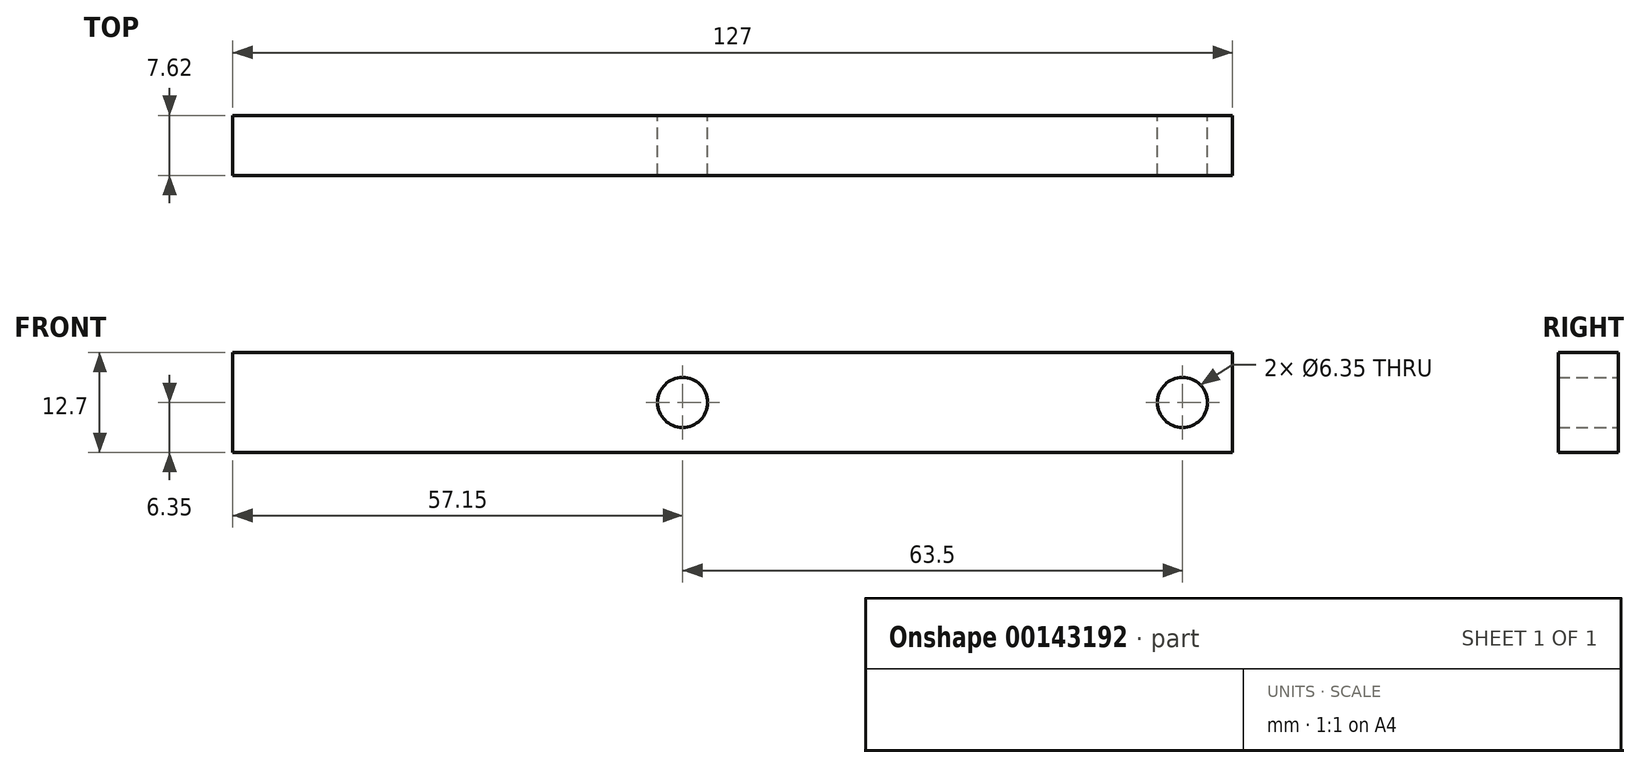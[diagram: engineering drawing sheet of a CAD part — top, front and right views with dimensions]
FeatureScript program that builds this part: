
annotation { "Feature Type Name" : "Feature", "Feature Type Description" : "" }
export const myFeature = defineFeature(function(context is Context, id is Id, definition is map)
    precondition{}
    {
        {
            var Q0;
            Q0=qCreatedBy(makeId("Front.planeOp"),FACE);
            var sketch = newSketch(context, id + "F0", { "sketchPlane" : qUnion([Q0])});
            skLineSegment(sketch, "E0.bottom", {"start": v(0, 0) * mm, "end": v(127, 0) * mm});
            skLineSegment(sketch, "E0.top", {"start": v(0, 12.7) * mm, "end": v(127, 12.7) * mm});
            skLineSegment(sketch, "E0.left", {"start": v(0, 0) * mm, "end": v(0, 12.7) * mm});
            skLineSegment(sketch, "E0.right", {"start": v(127, 0) * mm, "end": v(127, 12.7) * mm});
            skCircle(sketch, "E1", {"center": v(57.15, 6.35) * mm, "radius": 3.18 * mm});
            skCircle(sketch, "E2", {"center": v(120.65, 6.35) * mm, "radius": 3.18 * mm});
            skSolve(sketch);
        }
        {
            var Q0;
            Q0=makeQuery(id+"F0.imprint","IMPRINT",FACE,{"disambiguationData":[TD([[makeQuery(id+"F0.imprint","IMPRINT",EDGE,{"derivedFrom":sQuery(id+"F0.wireOp",EDGE,"E0.bottom")}),1.0]])]});
            extrude(context, id + "F1", {"entities" : qUnion([Q0]), "depth" : 7.62 * mm});
        }
    });
